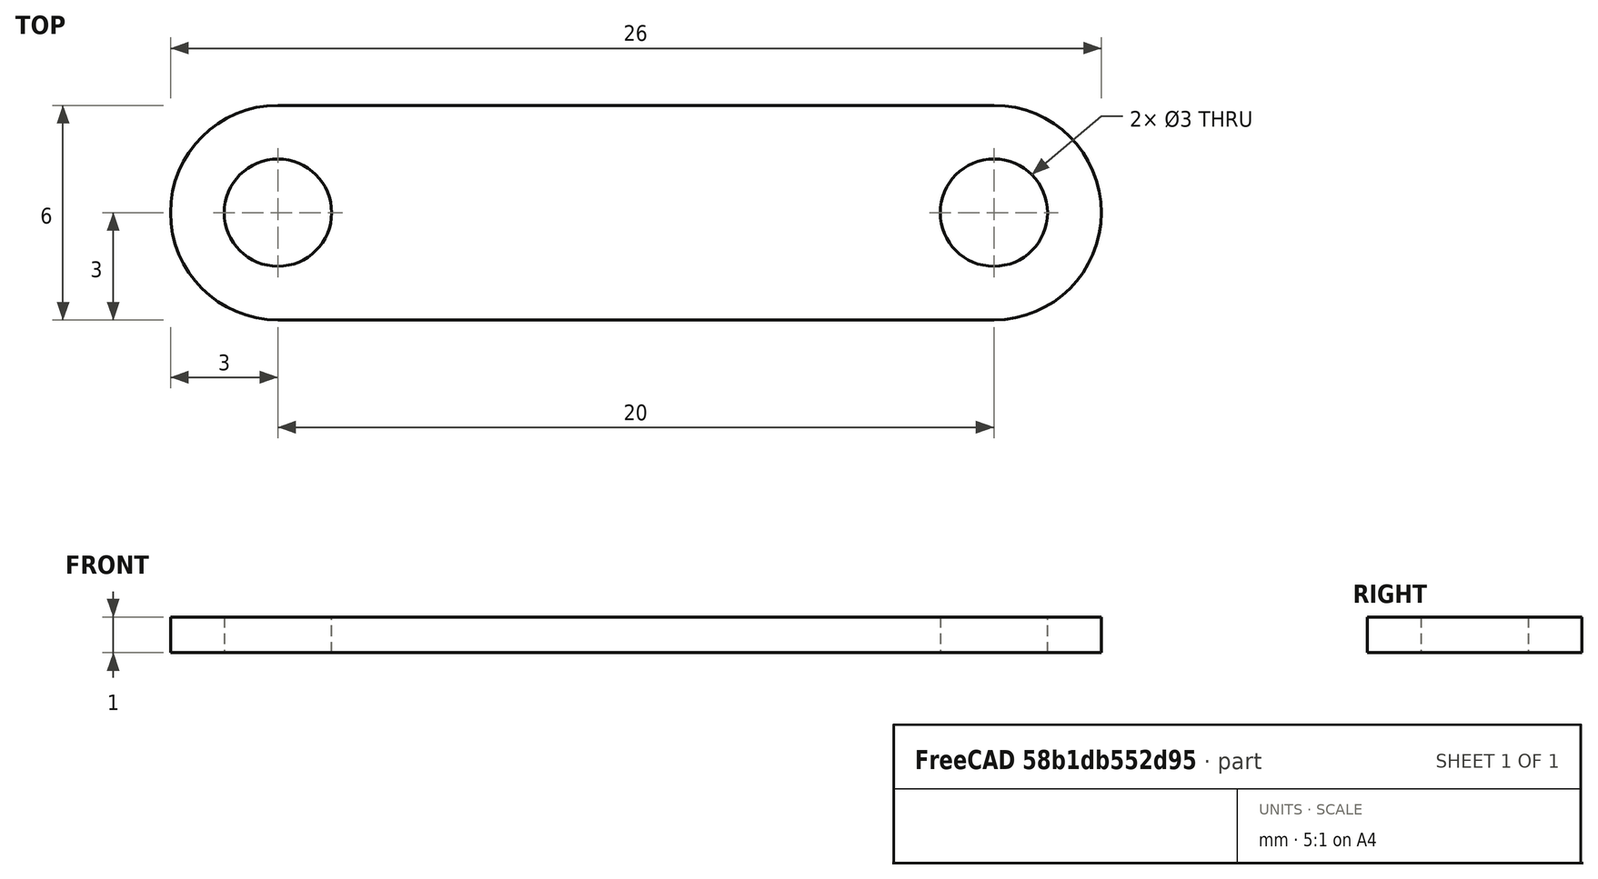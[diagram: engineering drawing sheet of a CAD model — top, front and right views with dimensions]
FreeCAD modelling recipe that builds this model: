
FCSTD DOCUMENT  (FreeCAD 0.18.3R)
Label: pcb-clip
License: CreativeCommons Attribution
LicenseURL: http://creativecommons.org/licenses/by/4.0/
objects: Sketcher::SketchObject×1, PartDesign::Pad×1, PartDesign::Body×1
note: 4 computed .brp shape members not serialized (recipe doc carries the construction recipe); baked Part::Feature solids carry a one-line shape summary decoded from their .brp

FEATURE [Sketcher::SketchObject] Sketch
  MapMode = 5
  Support = -> [XY_Plane]
  sketch-geometry (6):
    g0: ArcOfCircle CenterX=-10 CenterY=0 CenterZ=0 NormalX=0 NormalY=0 NormalZ=1 AngleXU=0 Radius=3 StartAngle=1.5708 EndAngle=4.71239
    g1: ArcOfCircle CenterX=10 CenterY=0 CenterZ=0 NormalX=0 NormalY=0 NormalZ=1 AngleXU=0 Radius=3 StartAngle=4.71239 EndAngle=7.85398
    g2: LineSegment StartX=-10 StartY=-3 StartZ=0 EndX=10 EndY=-3 EndZ=0
    g3: LineSegment StartX=-10 StartY=3 StartZ=0 EndX=10 EndY=3 EndZ=0
    g4: Circle CenterX=-10 CenterY=0 CenterZ=0 NormalX=0 NormalY=0 NormalZ=1 AngleXU=0 Radius=1.5
    g5: Circle CenterX=10 CenterY=0 CenterZ=0 NormalX=0 NormalY=0 NormalZ=1 AngleXU=0 Radius=1.5
  constraints (13):
    c: Tangent(g0,g3) = 1.5708
    c: Tangent(g0,g2) = -1.5708
    c: Tangent(g2,g1) = -1.5708
    c: Tangent(g3,g1) = 1.5708
    c: Horizontal(g2)
    c: Coincident(g4,g0)
    c: Coincident(g5,g1)
    c: PointOnObject(g0,g-1)
    c: Symmetric(g0,g1,g-2)
    c: Equal(g5,g4)
    c: DistanceX(g0,g1) = 20
    c: Radius(g5) = 1.5
    c: Radius(g1) = 3
FEATURE [PartDesign::Pad] Pad
  Length = 1
  Length2 = 100
  Profile = -> Sketch
  Refine = true
  Type = 0
FEATURE [PartDesign::Body] Body
  Group = -> [Sketch,Pad]
  Origin = -> Origin
  Tip = -> Pad
